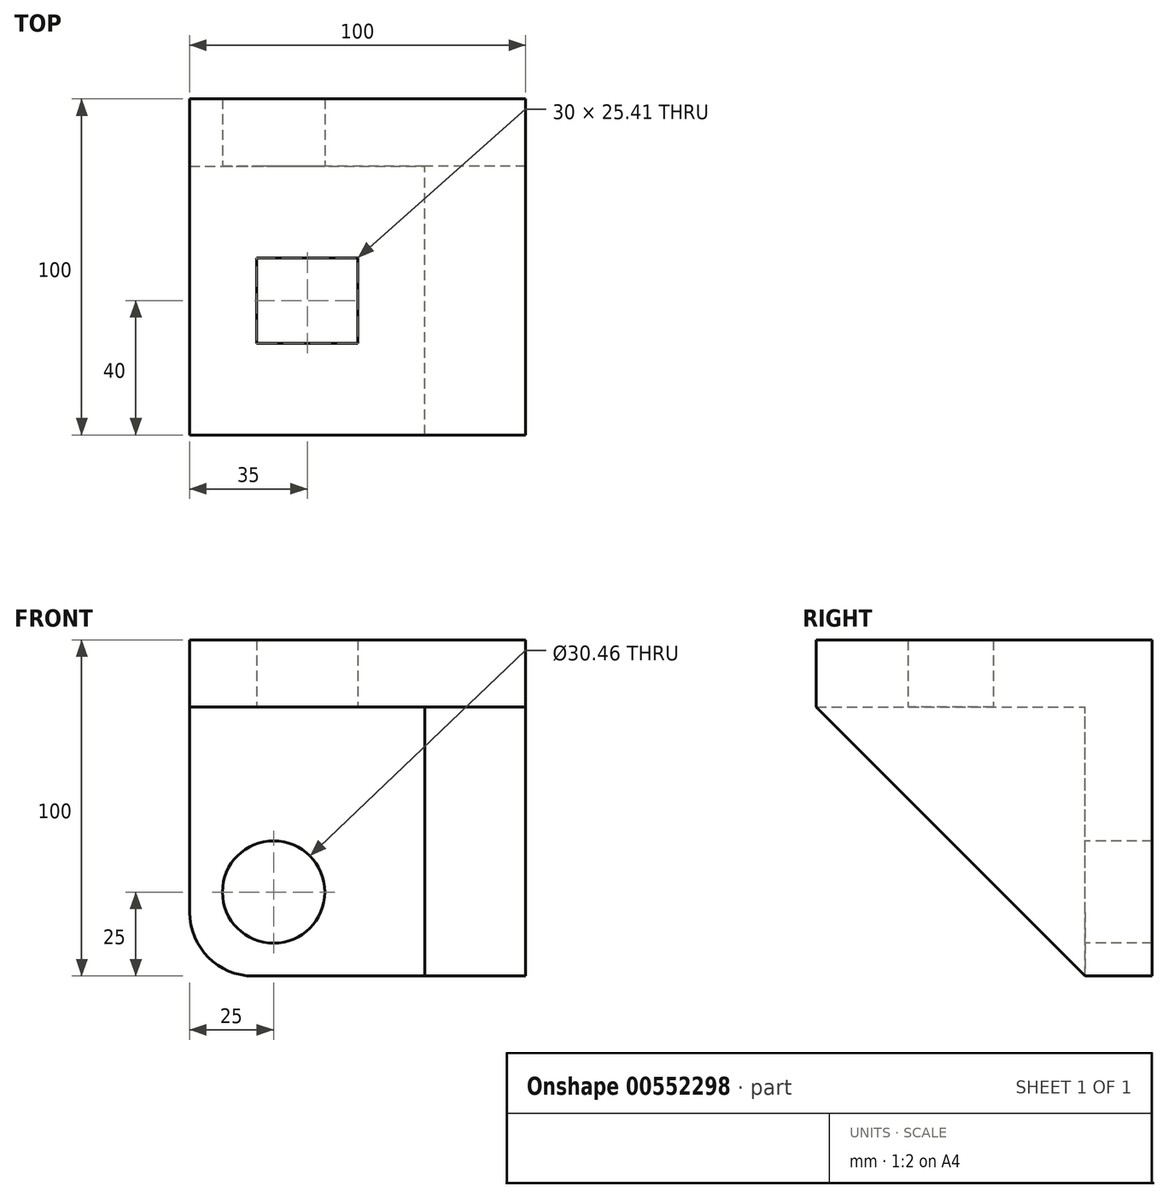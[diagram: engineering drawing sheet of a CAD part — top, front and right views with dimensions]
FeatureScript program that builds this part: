
annotation { "Feature Type Name" : "Feature", "Feature Type Description" : "" }
export const myFeature = defineFeature(function(context is Context, id is Id, definition is map)
    precondition{}
    {
        {
            var Q0;
            Q0=qCreatedBy(makeId("Front.planeOp"),FACE);
            var sketch = newSketch(context, id + "F0", { "sketchPlane" : qUnion([Q0])});
            skLineSegment(sketch, "E0.bottom", {"start": v(50, -50) * mm, "end": v(-50, -50) * mm});
            skLineSegment(sketch, "E0.top", {"start": v(50, 50) * mm, "end": v(-50, 50) * mm});
            skLineSegment(sketch, "E0.left", {"start": v(50, -50) * mm, "end": v(50, 50) * mm});
            skLineSegment(sketch, "E0.right", {"start": v(-50, -50) * mm, "end": v(-50, 50) * mm});
            skPoint(sketch, "E0.middle", {"position": v(0, 0) * mm});
            skSolve(sketch);
        }
        {
            var Q0;
            Q0=makeQuery(id+"F0.imprint","IMPRINT",FACE,{"disambiguationData":[TD([[makeQuery(id+"F0.imprint","IMPRINT",EDGE,{"derivedFrom":sQuery(id+"F0.wireOp",EDGE,"E0.bottom")}),-1.0]])]});
            extrude(context, id + "F1", {"entities" : qUnion([Q0]), "depth" : 20 * mm, "offsetDistance" : 25.4 * mm});
        }
        {
            var Q0;
            Q0=makeQuery(id+"F1.opExtrude","CAP_FACE",FACE,{"disambiguationData":[OSD([sQuery(id+"F0.wireOp",EDGE,"E0.bottom"),sQuery(id+"F0.wireOp",EDGE,"E0.top"),sQuery(id+"F0.wireOp",EDGE,"E0.left"),sQuery(id+"F0.wireOp",EDGE,"E0.right")])],"isStart":false});
            var sketch = newSketch(context, id + "F2", { "sketchPlane" : qUnion([Q0])});
            skLineSegment(sketch, "E1.bottom", {"start": v(-50, 50) * mm, "end": v(50, 50) * mm});
            skLineSegment(sketch, "E1.top", {"start": v(-50, 30) * mm, "end": v(50, 30) * mm});
            skLineSegment(sketch, "E1.left", {"start": v(-50, 50) * mm, "end": v(-50, 30) * mm});
            skLineSegment(sketch, "E1.right", {"start": v(50, 50) * mm, "end": v(50, 30) * mm});
            skSolve(sketch);
        }
        {
            var Q0;
            Q0=makeQuery(id+"F2.imprint","IMPRINT",FACE,{"disambiguationData":[TD([[makeQuery(id+"F2.imprint","IMPRINT",EDGE,{"derivedFrom":sQuery(id+"F2.wireOp",EDGE,"E1.bottom")}),1.0]])]});
            extrude(context, id + "F3", {"entities" : qUnion([Q0]), "operationType" : NewBodyOperationType.ADD, "depth" : 80 * mm, "offsetDistance" : 25.4 * mm});
        }
        {
            var Q0;
            Q0=makeQuery(id+"F1.opExtrude","CAP_FACE",FACE,{"disambiguationData":[OSD([sQuery(id+"F0.wireOp",EDGE,"E0.bottom"),sQuery(id+"F0.wireOp",EDGE,"E0.top"),sQuery(id+"F0.wireOp",EDGE,"E0.left"),sQuery(id+"F0.wireOp",EDGE,"E0.right")])],"isStart":false});
            var sketch = newSketch(context, id + "F4", { "sketchPlane" : qUnion([Q0])});
            skLineSegment(sketch, "E2.bottom", {"start": v(50, -50) * mm, "end": v(20, -50) * mm});
            skLineSegment(sketch, "E2.top", {"start": v(50, 30) * mm, "end": v(20, 30) * mm});
            skLineSegment(sketch, "E2.left", {"start": v(50, -50) * mm, "end": v(50, 30) * mm});
            skLineSegment(sketch, "E2.right", {"start": v(20, -50) * mm, "end": v(20, 30) * mm});
            skSolve(sketch);
        }
        {
            var Q0;
            Q0=makeQuery(id+"F4.imprint","IMPRINT",FACE,{"disambiguationData":[TD([[makeQuery(id+"F4.imprint","IMPRINT",EDGE,{"derivedFrom":sQuery(id+"F4.wireOp",EDGE,"E2.bottom")}),-1.0]])]});
            extrude(context, id + "F5", {"entities" : qUnion([Q0]), "operationType" : NewBodyOperationType.ADD, "depth" : 80 * mm, "offsetDistance" : 25.4 * mm});
        }
        {
            var Q0;
            Q0=makeQuery(id+"F5.opExtrude","CAP_EDGE",EDGE,{"disambiguationData":[OSD([sQuery(id+"F4.wireOp",EDGE,"E2.bottom")])],"isStart":false});
            chamfer(context, id + "F6", {"entities" : qUnion([Q0]), "chamferType" : ChamferType.OFFSET_ANGLE, "width" : 80 * mm, "oppositeDirection" : false, "angle" : 45 * degree, "tangentPropagation" : true});
        }
        {
            var Q0;
            Q0=makeQuery(id+"F3.opExtrude","SWEPT_FACE",FACE,{"disambiguationData":[OSD([sQuery(id+"F2.wireOp",EDGE,"E1.top")])]});
            var sketch = newSketch(context, id + "F7", { "sketchPlane" : qUnion([Q0])});
            skLineSegment(sketch, "E3", {"start": v(-15, 100) * mm, "end": v(-15, 20) * mm});
            skLineSegment(sketch, "E4", {"start": v(-50, 60) * mm, "end": v(20, 60) * mm});
            skLineSegment(sketch, "E5.bottom", {"start": v(0, 47.3) * mm, "end": v(-30, 47.3) * mm});
            skLineSegment(sketch, "E5.top", {"start": v(0, 72.7) * mm, "end": v(-30, 72.7) * mm});
            skLineSegment(sketch, "E5.left", {"start": v(0, 47.3) * mm, "end": v(0, 72.7) * mm});
            skLineSegment(sketch, "E5.right", {"start": v(-30, 47.3) * mm, "end": v(-30, 72.7) * mm});
            skPoint(sketch, "E5.middle", {"position": v(-15, 60) * mm});
            skSolve(sketch);
        }
        {
            var Q0;
            {var subQ0=sQuery(id+"F7.wireOp",EDGE,"E5.top");var subQ1=sQuery(id+"F7.wireOp",EDGE,"E3");var subQ2=makeQuery(id+"F7.imprint","INTERSECT",VERTEX,{"derivedFrom":[subQ1,subQ0]});Q0=makeQuery(id+"F7.imprint","IMPRINT",FACE,{"disambiguationData":[TD([[makeQuery(id+"F7.imprint","IMPRINT",EDGE,{"disambiguationData":[TD([[subQ2,-1.0]])],"derivedFrom":subQ1}),-1.0]])]});}
            var Q1;
            {var subQ0=sQuery(id+"F7.wireOp",EDGE,"E4");var subQ1=sQuery(id+"F7.wireOp",EDGE,"E3");var subQ2=makeQuery(id+"F7.imprint","INTERSECT",VERTEX,{"derivedFrom":[subQ1,subQ0]});Q1=makeQuery(id+"F7.imprint","IMPRINT",FACE,{"disambiguationData":[TD([[makeQuery(id+"F7.imprint","IMPRINT",EDGE,{"disambiguationData":[TD([[subQ2,-1.0]])],"derivedFrom":subQ1}),-1.0]])]});}
            var Q2;
            {var subQ0=sQuery(id+"F7.wireOp",EDGE,"E4");var subQ1=sQuery(id+"F7.wireOp",EDGE,"E3");var subQ2=makeQuery(id+"F7.imprint","INTERSECT",VERTEX,{"derivedFrom":[subQ1,subQ0]});Q2=makeQuery(id+"F7.imprint","IMPRINT",FACE,{"disambiguationData":[TD([[makeQuery(id+"F7.imprint","IMPRINT",EDGE,{"disambiguationData":[TD([[subQ2,-1.0]])],"derivedFrom":subQ1}),1.0]])]});}
            var Q3;
            {var subQ0=sQuery(id+"F7.wireOp",EDGE,"E5.top");var subQ1=sQuery(id+"F7.wireOp",EDGE,"E3");var subQ2=makeQuery(id+"F7.imprint","INTERSECT",VERTEX,{"derivedFrom":[subQ1,subQ0]});Q3=makeQuery(id+"F7.imprint","IMPRINT",FACE,{"disambiguationData":[TD([[makeQuery(id+"F7.imprint","IMPRINT",EDGE,{"disambiguationData":[TD([[subQ2,-1.0]])],"derivedFrom":subQ1}),1.0]])]});}
            extrude(context, id + "F8", {"entities" : qUnion([Q0, Q1, Q2, Q3]), "operationType" : NewBodyOperationType.REMOVE, "oppositeDirection" : true, "depth" : 127 * mm, "offsetDistance" : 25.4 * mm});
        }
        {
            var Q0;
            Q0=makeQuery(id+"F1.opExtrude","CAP_FACE",FACE,{"disambiguationData":[OSD([sQuery(id+"F0.wireOp",EDGE,"E0.bottom"),sQuery(id+"F0.wireOp",EDGE,"E0.top"),sQuery(id+"F0.wireOp",EDGE,"E0.left"),sQuery(id+"F0.wireOp",EDGE,"E0.right")])],"isStart":false});
            var sketch = newSketch(context, id + "F9", { "sketchPlane" : qUnion([Q0])});
            skLineSegment(sketch, "E6", {"start": v(-50, -50) * mm, "end": v(-50, -25) * mm});
            skLineSegment(sketch, "E7", {"start": v(-50, -25) * mm, "end": v(-25, -25) * mm});
            skLineSegment(sketch, "E8", {"start": v(-50, -50) * mm, "end": v(-25, -50) * mm});
            skLineSegment(sketch, "E9", {"start": v(-25, -50) * mm, "end": v(-25, -25) * mm});
            skCircle(sketch, "E10", {"center": v(-25, -25) * mm, "radius": 15 * mm});
            skSolve(sketch);
        }
        {
            var Q0;
            {var subQ0=sQuery(id+"F9.wireOp",EDGE,"E9");var subQ1=sQuery(id+"F9.wireOp",EDGE,"E7");var subQ2=makeQuery(id+"F9.imprint","INTERSECT",VERTEX,{"derivedFrom":[subQ1,subQ0]});Q0=makeQuery(id+"F9.imprint","IMPRINT",FACE,{"disambiguationData":[TD([[makeQuery(id+"F9.imprint","IMPRINT",EDGE,{"disambiguationData":[TD([[subQ2,1.0]])],"derivedFrom":subQ1}),-1.0]])]});}
            extrude(context, id + "F10", {"entities" : qUnion([Q0]), "operationType" : NewBodyOperationType.REMOVE, "oppositeDirection" : true, "depth" : 1143 * mm, "offsetDistance" : 25.4 * mm});
        }
        {
            var Q0;
            Q0=makeQuery(id+"F1.opExtrude","CAP_FACE",FACE,{"disambiguationData":[OSD([sQuery(id+"F0.wireOp",EDGE,"E0.bottom"),sQuery(id+"F0.wireOp",EDGE,"E0.top"),sQuery(id+"F0.wireOp",EDGE,"E0.left"),sQuery(id+"F0.wireOp",EDGE,"E0.right")])],"isStart":false});
            var sketch = newSketch(context, id + "F11", { "sketchPlane" : qUnion([Q0])});
            skCircle(sketch, "E11", {"center": v(-25, -25) * mm, "radius": 15.23 * mm});
            skSolve(sketch);
        }
        {
            var Q0;
            Q0 = qSketchRegion(id + "F11", true);
            var Q1;
            Q1=makeQuery(id+"F11.imprint","IMPRINT",FACE,{"disambiguationData":[TD([[makeQuery(id+"F11.imprint","IMPRINT",EDGE,{"derivedFrom":sQuery(id+"F11.wireOp",EDGE,"E11")}),1.0]])]});
            extrude(context, id + "F12", {"entities" : qUnion([Q0, Q1]), "operationType" : NewBodyOperationType.REMOVE, "oppositeDirection" : true, "depth" : 254 * mm, "offsetDistance" : 25.4 * mm});
        }
        {
            var Q0;
            Q0=makeQuery(id+"F1.opExtrude","SWEPT_EDGE",EDGE,{"disambiguationData":[OSD([sQuery(id+"F0.wireOp",EDGE,"E0.bottom"),sQuery(id+"F0.wireOp",EDGE,"E0.right")])]});
            fillet(context, id + "F13", {"entities" : qUnion([Q0]), "radius" : 19 * mm, "tangentPropagation" : true, "allowEdgeOverflow" : false});
        }
    });
